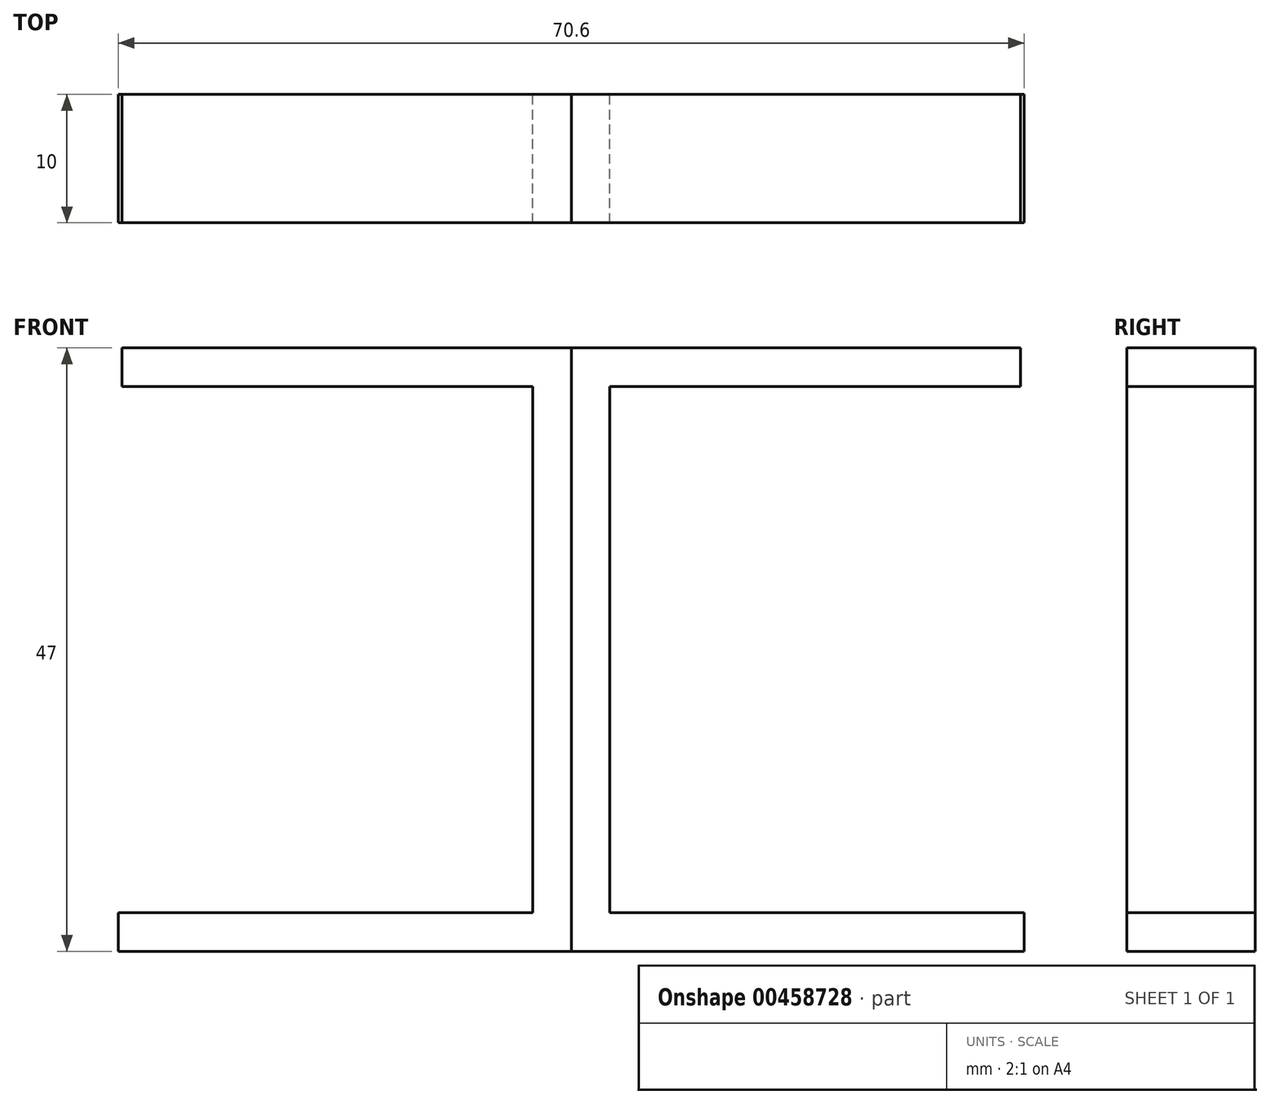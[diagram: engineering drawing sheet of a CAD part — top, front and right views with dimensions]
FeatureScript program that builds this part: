
annotation { "Feature Type Name" : "Feature", "Feature Type Description" : "" }
export const myFeature = defineFeature(function(context is Context, id is Id, definition is map)
    precondition{}
    {
        {
            var Q0;
            Q0=qCreatedBy(makeId("Front.planeOp"),FACE);
            var sketch = newSketch(context, id + "F0", { "sketchPlane" : qUnion([Q0])});
            skLineSegment(sketch, "E0.bottom", {"start": v(-33.01, 32.86) * mm, "end": v(1.99, 32.86) * mm});
            skLineSegment(sketch, "E0.top", {"start": v(-33.01, 29.86) * mm, "end": v(1.99, 29.86) * mm});
            skLineSegment(sketch, "E0.left", {"start": v(-33.01, 32.86) * mm, "end": v(-33.01, 29.86) * mm});
            skLineSegment(sketch, "E0.right", {"start": v(1.99, 32.86) * mm, "end": v(1.99, 29.86) * mm});
            skLineSegment(sketch, "E1.bottom", {"start": v(1.99, 32.86) * mm, "end": v(-1.01, 32.86) * mm});
            skLineSegment(sketch, "E1.top", {"start": v(1.99, -14.14) * mm, "end": v(-1.01, -14.14) * mm});
            skLineSegment(sketch, "E1.left", {"start": v(1.99, 32.86) * mm, "end": v(1.99, -14.14) * mm});
            skLineSegment(sketch, "E1.right", {"start": v(-1.01, 32.86) * mm, "end": v(-1.01, -14.14) * mm});
            skLineSegment(sketch, "E2.bottom", {"start": v(1.99, -14.14) * mm, "end": v(-33.31, -14.14) * mm});
            skLineSegment(sketch, "E2.top", {"start": v(1.99, -11.14) * mm, "end": v(-33.31, -11.14) * mm});
            skLineSegment(sketch, "E2.left", {"start": v(1.99, -14.14) * mm, "end": v(1.99, -11.14) * mm});
            skLineSegment(sketch, "E2.right", {"start": v(-33.31, -14.14) * mm, "end": v(-33.31, -11.14) * mm});
            skSolve(sketch);
        }
        {
            var Q0;
            Q0 = qSketchRegion(id + "F0", true);
            extrude(context, id + "F1", {"entities" : qUnion([Q0]), "depth" : 10 * mm, "offsetDistance" : 25 * mm});
        }
        {
            var Q0;
            Q0=makeQuery(id+"F1.opExtrude","SWEPT_BODY",BODY,{"disambiguationData":[OSD([sQuery(id+"F0.wireOp",EDGE,"E0.bottom"),sQuery(id+"F0.wireOp",EDGE,"E0.top"),sQuery(id+"F0.wireOp",EDGE,"E0.left"),sQuery(id+"F0.wireOp",EDGE,"E1.bottom"),sQuery(id+"F0.wireOp",EDGE,"E1.left"),sQuery(id+"F0.wireOp",EDGE,"E1.right"),sQuery(id+"F0.wireOp",EDGE,"E2.bottom"),sQuery(id+"F0.wireOp",EDGE,"E2.top"),sQuery(id+"F0.wireOp",EDGE,"E2.left"),sQuery(id+"F0.wireOp",EDGE,"E2.right")])]});
            var Q1;
            Q1=makeQuery(id+"F1.opExtrude","SWEPT_FACE",FACE,{"disambiguationData":[OSD([sQuery(id+"F0.wireOp",EDGE,"E1.left"),sQuery(id+"F0.wireOp",EDGE,"E2.left")])]});
            mirror(context, id + "F2", {"entities" : qUnion([Q0]), "mirrorPlane" : qUnion([Q1])});
        }
    });
